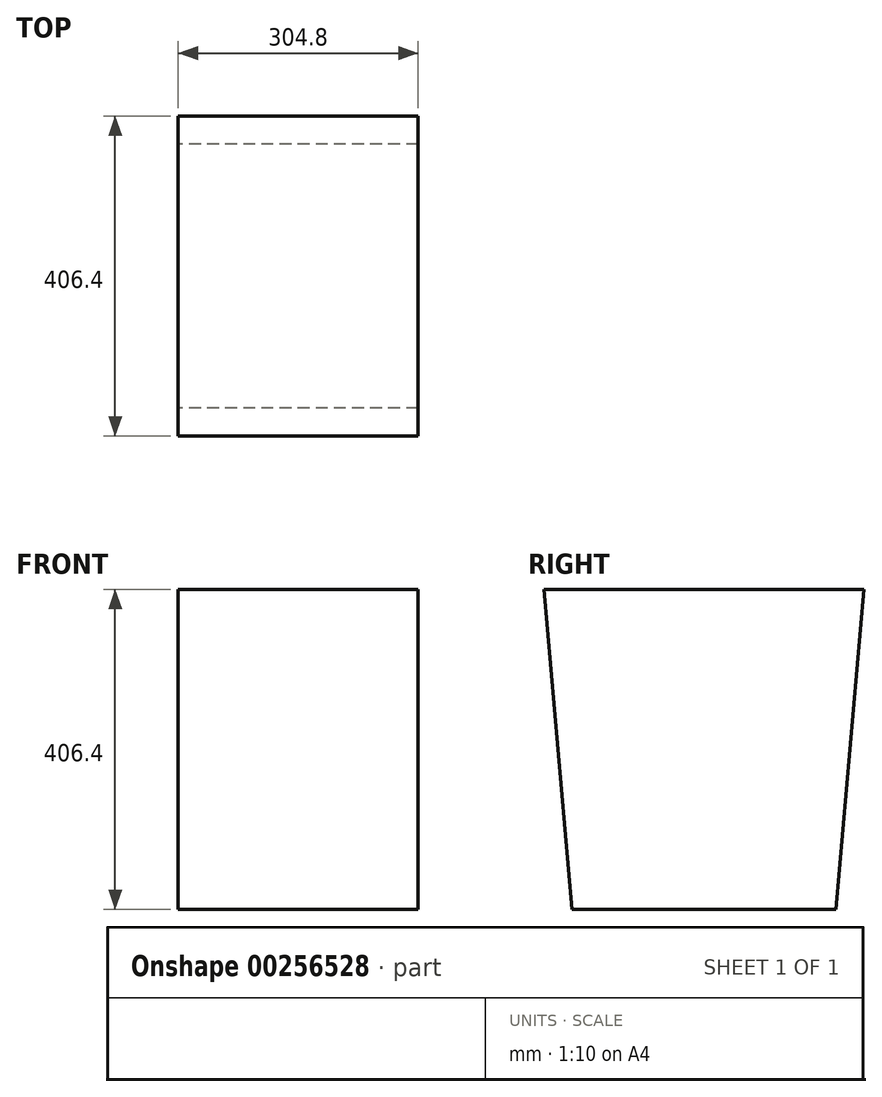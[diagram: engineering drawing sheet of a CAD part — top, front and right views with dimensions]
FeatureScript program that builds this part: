
annotation { "Feature Type Name" : "Feature", "Feature Type Description" : "" }
export const myFeature = defineFeature(function(context is Context, id is Id, definition is map)
    precondition{}
    {
        {
            var Q0;
            Q0=qCreatedBy(makeId("Top.planeOp"),FACE);
            var sketch = newSketch(context, id + "F0", { "sketchPlane" : qUnion([Q0])});
            skLineSegment(sketch, "E0.bottom", {"start": v(152.4, -203.2) * mm, "end": v(-152.4, -203.2) * mm});
            skLineSegment(sketch, "E0.top", {"start": v(152.4, 203.2) * mm, "end": v(-152.4, 203.2) * mm});
            skLineSegment(sketch, "E0.left", {"start": v(152.4, -203.2) * mm, "end": v(152.4, 203.2) * mm});
            skLineSegment(sketch, "E0.right", {"start": v(-152.4, -203.2) * mm, "end": v(-152.4, 203.2) * mm});
            skPoint(sketch, "E0.middle", {"position": v(0, 0) * mm});
            skSolve(sketch);
        }
        {
            var Q0;
            Q0=makeQuery(id+"F0.imprint","IMPRINT",FACE,{"disambiguationData":[TD([[makeQuery(id+"F0.imprint","IMPRINT",EDGE,{"derivedFrom":sQuery(id+"F0.wireOp",EDGE,"E0.bottom")}),-1.0]])]});
            extrude(context, id + "F1", {"entities" : qUnion([Q0]), "depth" : 406.4 * mm, "offsetDistance" : 25.4 * mm});
        }
        {
            var Q0;
            Q0=makeQuery(id+"F1.opExtrude","SWEPT_FACE",FACE,{"disambiguationData":[OSD([sQuery(id+"F0.wireOp",EDGE,"E0.right")])]});
            var sketch = newSketch(context, id + "F2", { "sketchPlane" : qUnion([Q0])});
            skPoint(sketch, "E1", {"position": v(-203.2, 406.4) * mm});
            skPoint(sketch, "E2", {"position": v(203.2, 406.4) * mm});
            skLineSegment(sketch, "E3", {"start": v(-203.2, 406.4) * mm, "end": v(-167.64, 0) * mm});
            skLineSegment(sketch, "E4", {"start": v(203.2, 406.4) * mm, "end": v(167.64, 0) * mm});
            skSolve(sketch);
        }
        {
            var Q0;
            {var subQ0=sQuery(id+"F2.wireOp",EDGE,"E3");Q0=makeQuery(id+"F2.imprint","IMPRINT",FACE,{"disambiguationData":[TD([[makeQuery(id+"F2.imprint","IMPRINT",EDGE,{"derivedFrom":subQ0}),-1.0]])]});}
            extrude(context, id + "F3", {"entities" : qUnion([Q0]), "operationType" : NewBodyOperationType.REMOVE, "oppositeDirection" : true, "depth" : 609.6 * mm, "offsetDistance" : 25.4 * mm});
        }
        {
            var Q0;
            {var subQ0=sQuery(id+"F2.wireOp",EDGE,"E4");Q0=makeQuery(id+"F2.imprint","IMPRINT",FACE,{"disambiguationData":[TD([[makeQuery(id+"F2.imprint","IMPRINT",EDGE,{"derivedFrom":subQ0}),1.0]])]});}
            extrude(context, id + "F4", {"entities" : qUnion([Q0]), "operationType" : NewBodyOperationType.REMOVE, "oppositeDirection" : true, "depth" : 609.6 * mm, "offsetDistance" : 25.4 * mm});
        }
    });
